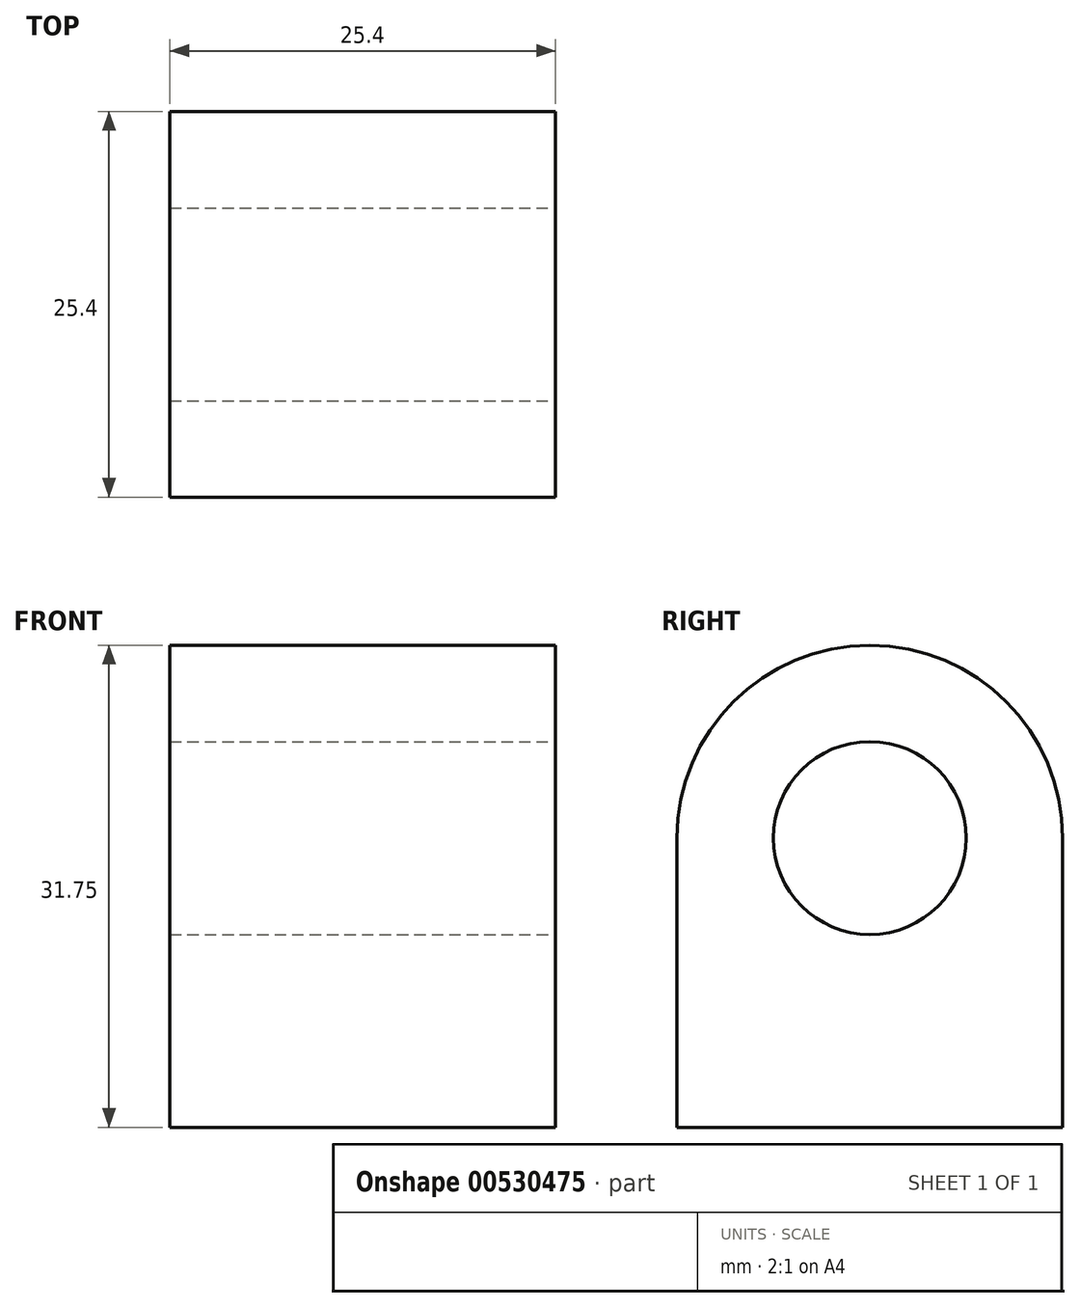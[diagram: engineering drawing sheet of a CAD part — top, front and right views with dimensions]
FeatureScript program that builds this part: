
annotation { "Feature Type Name" : "Feature", "Feature Type Description" : "" }
export const myFeature = defineFeature(function(context is Context, id is Id, definition is map)
    precondition{}
    {
        {
            var Q0;
            Q0=qCreatedBy(makeId("Front.planeOp"),FACE);
            var sketch = newSketch(context, id + "F0", { "sketchPlane" : qUnion([Q0])});
            skLineSegment(sketch, "E0", {"start": v(-60.71, 0) * mm, "end": v(-60.71, 12.7) * mm});
            skLineSegment(sketch, "E1", {"start": v(-60.71, 12.7) * mm, "end": v(-35.31, 12.7) * mm});
            skLineSegment(sketch, "E2", {"start": v(-35.31, 12.7) * mm, "end": v(-35.31, 44.45) * mm});
            skLineSegment(sketch, "E3", {"start": v(-35.31, 44.45) * mm, "end": v(-9.91, 44.45) * mm});
            skLineSegment(sketch, "E4", {"start": v(-9.91, 44.45) * mm, "end": v(-9.91, 12.7) * mm});
            skLineSegment(sketch, "E5", {"start": v(-9.91, 12.7) * mm, "end": v(21.84, 12.7) * mm});
            skLineSegment(sketch, "E6", {"start": v(21.84, 12.7) * mm, "end": v(21.84, 0) * mm});
            skLineSegment(sketch, "E7", {"start": v(21.84, 0) * mm, "end": v(-60.71, 0) * mm});
            skSolve(sketch);
        }
        {
            var Q0;
            Q0 = qSketchRegion(id + "F0", true);
            extrude(context, id + "F1", {"entities" : qUnion([Q0]), "depth" : 25.4 * mm, "offsetDistance" : 25.4 * mm});
        }
        {
            var Q0;
            Q0=makeQuery(id+"F1.opExtrude","SWEPT_FACE",FACE,{"disambiguationData":[OSD([sQuery(id+"F0.wireOp",EDGE,"E1")])]});
            var sketch = newSketch(context, id + "F2", { "sketchPlane" : qUnion([Q0])});
            skCircle(sketch, "E8", {"center": v(-48.01, -12.7) * mm, "radius": 6.35 * mm});
            skCircle(sketch, "E9", {"center": v(2.97, -12.7) * mm, "radius": 6.35 * mm});
            skArc(sketch, "E10", {"start": v(-48.01, 0) * mm, "mid": v(-60.71, -12.7) * mm, "end": v(-48.01, -25.4) * mm});
            skArc(sketch, "E11", {"start": v(2.97, -25.4) * mm, "mid": v(15.67, -12.7) * mm, "end": v(2.97, 0) * mm});
            skLineSegment(sketch, "E12", {"start": v(2.97, -25.4) * mm, "end": v(21.78, -25.4) * mm});
            skLineSegment(sketch, "E13", {"start": v(21.78, -25.4) * mm, "end": v(21.78, 0) * mm});
            skLineSegment(sketch, "E14", {"start": v(21.78, 0) * mm, "end": v(2.97, 0) * mm});
            skSolve(sketch);
        }
        {
            var Q0;
            Q0=makeQuery(id+"F2.imprint","IMPRINT",FACE,{"disambiguationData":[TD([[makeQuery(id+"F2.imprint","IMPRINT",EDGE,{"derivedFrom":sQuery(id+"F2.wireOp",EDGE,"E11")}),-1.0]])]});
            var Q1;
            Q1=makeQuery(id+"F2.imprint","IMPRINT",FACE,{"disambiguationData":[TD([[makeQuery(id+"F2.imprint","IMPRINT",EDGE,{"derivedFrom":sQuery(id+"F2.wireOp",EDGE,"E9")}),1.0]])]});
            var Q2;
            Q2=makeQuery(id+"F2.imprint","IMPRINT",FACE,{"disambiguationData":[TD([[makeQuery(id+"F2.imprint","IMPRINT",EDGE,{"derivedFrom":sQuery(id+"F2.wireOp",EDGE,"E8")}),1.0]])]});
            var Q3;
            {var subQ0=sQuery(id+"F2.wireOp",EDGE,"E10");var subQ1=sQuery(id+"F0.wireOp",EDGE,"E1");var subQ2=makeQuery(id+"F1.opExtrude","CAP_EDGE",EDGE,{"disambiguationData":[OSD([subQ1])],"isStart":false});var subQ3=makeQuery(id+"F2.imprint","INTERSECT",VERTEX,{"derivedFrom":[subQ2,subQ0]});Q3=makeQuery(id+"F2.imprint","IMPRINT",FACE,{"disambiguationData":[TD([[makeQuery(id+"F2.imprint","IMPRINT",EDGE,{"disambiguationData":[TD([[subQ3,1.0]])],"derivedFrom":subQ0}),-1.0]])]});}
            var Q4;
            {var subQ0=sQuery(id+"F2.wireOp",EDGE,"E10");var subQ1=sQuery(id+"F0.wireOp",EDGE,"E1");var subQ2=makeQuery(id+"F1.opExtrude","CAP_EDGE",EDGE,{"disambiguationData":[OSD([subQ1])],"isStart":true});var subQ3=makeQuery(id+"F2.imprint","INTERSECT",VERTEX,{"derivedFrom":[subQ2,subQ0]});Q4=makeQuery(id+"F2.imprint","IMPRINT",FACE,{"disambiguationData":[TD([[makeQuery(id+"F2.imprint","IMPRINT",EDGE,{"disambiguationData":[TD([[subQ3,-1.0]])],"derivedFrom":subQ0}),-1.0]])]});}
            extrude(context, id + "F3", {"entities" : qUnion([Q0, Q1, Q2, Q3, Q4]), "operationType" : NewBodyOperationType.REMOVE, "oppositeDirection" : true, "depth" : 25.4 * mm, "offsetDistance" : 25.4 * mm});
        }
        {
            var Q0;
            Q0=makeQuery(id+"F1.opExtrude","SWEPT_FACE",FACE,{"disambiguationData":[OSD([sQuery(id+"F0.wireOp",EDGE,"E6")])]});
            extrude(context, id + "F4", {"entities" : qUnion([Q0]), "operationType" : NewBodyOperationType.REMOVE, "endBound" : BoundingType.THROUGH_ALL, "oppositeDirection" : true, "depth" : 25.4 * mm, "offsetDistance" : 25.4 * mm});
        }
        {
            var Q0;
            Q0=makeQuery(id+"F1.opExtrude","SWEPT_FACE",FACE,{"disambiguationData":[OSD([sQuery(id+"F0.wireOp",EDGE,"E4")])]});
            var sketch = newSketch(context, id + "F5", { "sketchPlane" : qUnion([Q0])});
            skCircle(sketch, "E15", {"center": v(-12.7, 31.75) * mm, "radius": 6.35 * mm});
            skArc(sketch, "E16", {"start": v(0, 31.75) * mm, "mid": v(-12.7, 44.45) * mm, "end": v(-25.4, 31.75) * mm});
            skSolve(sketch);
        }
        {
            var Q0;
            Q0 = qSketchRegion(id + "F5", true);
            var Q1;
            {var subQ0=sQuery(id+"F5.wireOp",EDGE,"E16");var subQ1=sQuery(id+"F0.wireOp",EDGE,"E4");var subQ2=makeQuery(id+"F1.opExtrude","CAP_EDGE",EDGE,{"disambiguationData":[OSD([subQ1])],"isStart":true});var subQ3=makeQuery(id+"F5.imprint","INTERSECT",VERTEX,{"derivedFrom":[subQ2,subQ0]});Q1=makeQuery(id+"F5.imprint","IMPRINT",FACE,{"disambiguationData":[TD([[makeQuery(id+"F5.imprint","IMPRINT",EDGE,{"disambiguationData":[TD([[subQ3,-1.0]])],"derivedFrom":subQ0}),-1.0]])]});}
            var Q2;
            {var subQ0=sQuery(id+"F5.wireOp",EDGE,"E16");var subQ1=sQuery(id+"F0.wireOp",EDGE,"E4");var subQ2=makeQuery(id+"F1.opExtrude","CAP_EDGE",EDGE,{"disambiguationData":[OSD([subQ1])],"isStart":false});var subQ3=makeQuery(id+"F5.imprint","INTERSECT",VERTEX,{"derivedFrom":[subQ2,subQ0]});Q2=makeQuery(id+"F5.imprint","IMPRINT",FACE,{"disambiguationData":[TD([[makeQuery(id+"F5.imprint","IMPRINT",EDGE,{"disambiguationData":[TD([[subQ3,1.0]])],"derivedFrom":subQ0}),-1.0]])]});}
            extrude(context, id + "F6", {"entities" : qUnion([Q0, Q1, Q2]), "operationType" : NewBodyOperationType.REMOVE, "oppositeDirection" : true, "depth" : 25.4 * mm, "offsetDistance" : 25.4 * mm});
        }
    });
